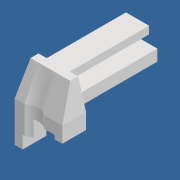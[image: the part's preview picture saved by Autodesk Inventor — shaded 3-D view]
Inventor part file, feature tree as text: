
AUTODESK INVENTOR PART (.ipt)
format: ipt  version: 2020 (Build 240168000, 168)  size: 241,664 bytes
history: native  units: mm
features: sketch x13, extrude x12, loft x1, other x1
ambient origin geometry x8: Origin, YZ Plane, XZ Plane, XY Plane, X Axis, Y Axis, Z Axis, Center Point
bodies: Solid1 (feature_tree)
feature tree (27):
  extrude  "Extrusion1"  Depth=88.0mm
  extrude  "Extrusion2"  Depth=23.4mm
  extrude  "Extrusion3"  Depth=15.8mm
  extrude  "Extrusion4"  TaperAngle=45.0deg  [1 undecoded]
  extrude  "Extrusion5"  Depth=8.0mm TaperAngle=0.0deg
  extrude  "Extrusion6"  Depth=15.8mm TaperAngle=0.0deg
  extrude  "Extrusion7"  Depth=24.0mm
  extrude  "Extrusion8"  Depth=12.0mm
  extrude  "Extrusion9"  Depth=7.8mm
  extrude  "Extrusion10"  Depth=5.0mm
  extrude  "Extrusion11"  Depth=4.2mm
  loft  "Loft1"
  extrude  "Extrusion12"  Depth=16.0mm
  sketch  "Sketch1"  dims[d0=40.0mm d1=88.0mm]
  sketch  "Sketch2"  dims[d2=11.4mm d3=0.0mm d4=23.4mm]
  sketch  "Sketch3"  dims[d5=7.5mm d6=15.8mm]
  sketch  "Sketch4"  dims[d7=8.3mm d8=45.0deg]
  sketch  "Sketch5"  dims[d9=135.0deg d10=8.0mm d11=0.0mm]
  sketch  "Sketch6"  dims[d12=8.0mm d13=15.8mm d14=0.0mm]
  sketch  "Sketch7"  dims[d15=8.0mm d16=24.0mm]
  sketch  "Sketch8"  dims[d17=12.0mm d18=0.0mm d19=12.0mm]
  sketch  "Sketch9"  dims[d20=8.0mm d21=0.0mm d22=7.8mm]
  sketch  "Sketch10"  dims[d23=3.8mm d24=0.0mm d25=5.0mm]
  sketch  "Sketch11"  dims[d26=5.0mm d27=4.2mm]
  sketch  "Sketch12"  dims[d28=16.0mm d29=4.0mm]
  other  "Edges1"
  sketch  "Sketch13"  dims[d30=8.0mm d31=0.0mm d32=16.0mm d33=16.0mm d34=0.0mm d35=8.0mm d36=12.8mm d37=0.0mm d38=4.4mm d39=16.4mm d40=10.0mm d41=4.0mm d42=10.2mm d43=0.0mm d44=10.0mm d45=10.0mm d46=16.0mm d47=0.0mm d48=0.0mm d49=0.0mm d50=90.0deg d51=0.0mm d52=90.0deg d53=4.6mm d54=3.8mm d55=4.6mm d56=16.0mm d57=16.0mm d58=0.0mm d60=4.6mm d62=4.6mm d63=16.0mm d65=24.0mm]
note: 1 required parameter value undecoded (feature->parameter linkage not recoverable at this tier; creation-order binding heuristic only, values carry confidence <= 0.55)
